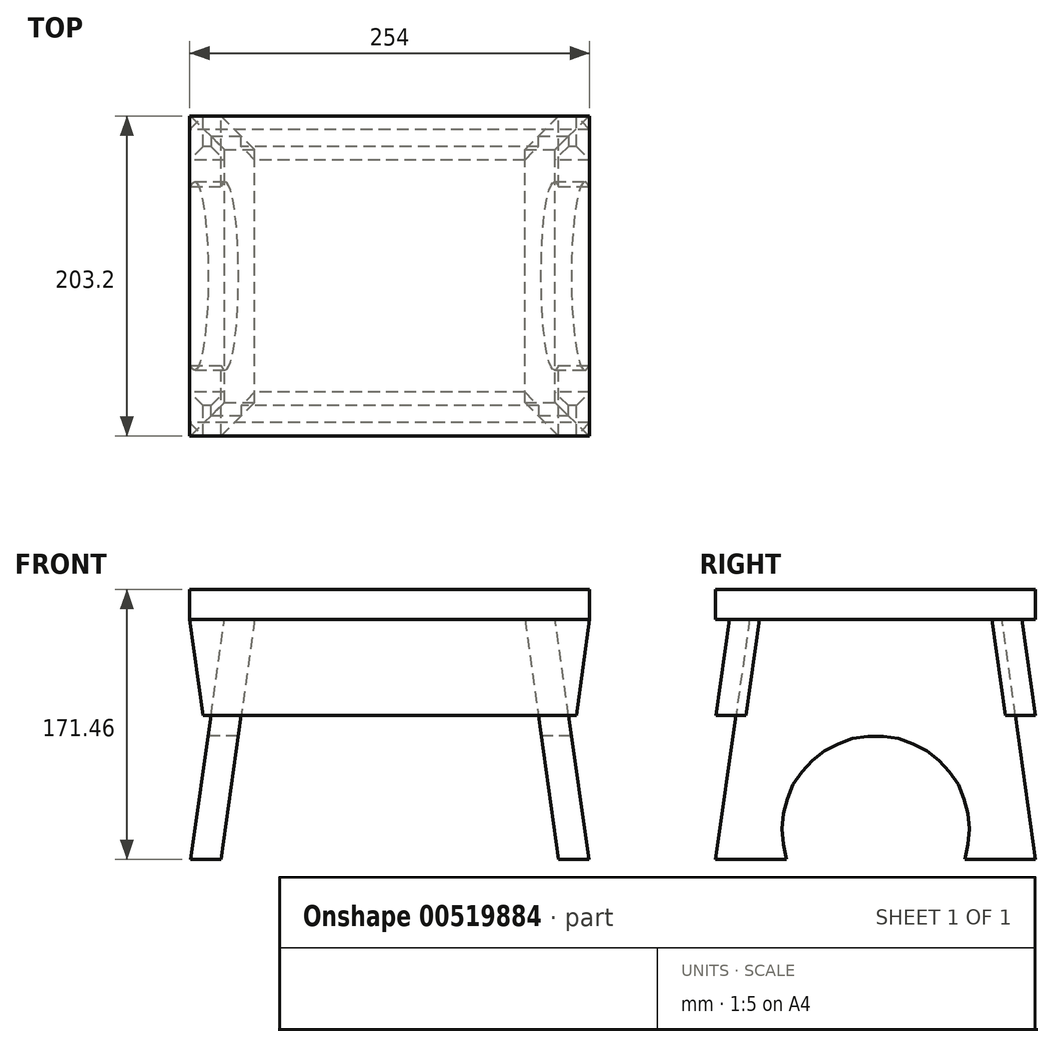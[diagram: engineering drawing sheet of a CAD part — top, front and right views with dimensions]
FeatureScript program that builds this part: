
annotation { "Feature Type Name" : "Feature", "Feature Type Description" : "" }
export const myFeature = defineFeature(function(context is Context, id is Id, definition is map)
    precondition{}
    {
        {
            var Q0;
            Q0=qCreatedBy(makeId("Front.planeOp"),FACE);
            var sketch = newSketch(context, id + "F0", { "sketchPlane" : qUnion([Q0])});
            skLineSegment(sketch, "E0.bottom", {"start": v(127, 9.53) * mm, "end": v(-127, 9.53) * mm});
            skLineSegment(sketch, "E0.top", {"start": v(127, -9.53) * mm, "end": v(-127, -9.53) * mm});
            skLineSegment(sketch, "E0.left", {"start": v(127, 9.53) * mm, "end": v(127, -9.52) * mm});
            skLineSegment(sketch, "E0.right", {"start": v(-127, 9.53) * mm, "end": v(-127, -9.52) * mm});
            skPoint(sketch, "E0.middle", {"position": v(0, 0) * mm});
            skLineSegment(sketch, "E1.bottom", {"start": v(-127, -9.53) * mm, "end": v(127, -9.53) * mm, "construction": true});
            skLineSegment(sketch, "E1.top", {"start": v(-127, -161.92) * mm, "end": v(127, -161.92) * mm, "construction": true});
            skLineSegment(sketch, "E1.left", {"start": v(-127, -9.52) * mm, "end": v(-127, -161.92) * mm, "construction": true});
            skLineSegment(sketch, "E1.right", {"start": v(127, -9.52) * mm, "end": v(127, -161.92) * mm, "construction": true});
            skLineSegment(sketch, "E2", {"start": v(105, -9.52) * mm, "end": v(126.42, -161.92) * mm});
            skLineSegment(sketch, "E3", {"start": v(126.42, -161.92) * mm, "end": v(107.18, -161.92) * mm});
            skLineSegment(sketch, "E4", {"start": v(107.18, -161.92) * mm, "end": v(85.76, -9.52) * mm});
            skLineSegment(sketch, "E5", {"start": v(0, -9.52) * mm, "end": v(0, -161.92) * mm});
            skLineSegment(sketch, "E6.MirrorCS", {"start": v(-107.18, -161.92) * mm, "end": v(-85.76, -9.52) * mm});
            skLineSegment(sketch, "E7.MirrorCS", {"start": v(-105, -9.52) * mm, "end": v(-126.42, -161.92) * mm});
            skLineSegment(sketch, "E8.MirrorCS", {"start": v(-126.42, -161.92) * mm, "end": v(-107.18, -161.92) * mm});
            skLineSegment(sketch, "E9.bottom", {"start": v(-127, -9.53) * mm, "end": v(127, -9.53) * mm});
            skLineSegment(sketch, "E9.top", {"start": v(-127, -70.48) * mm, "end": v(127, -70.48) * mm});
            skLineSegment(sketch, "E9.left", {"start": v(-127, -9.52) * mm, "end": v(-127, -70.48) * mm});
            skLineSegment(sketch, "E9.right", {"start": v(127, -9.52) * mm, "end": v(127, -70.48) * mm});
            skLineSegment(sketch, "E10", {"start": v(-127, -9.52) * mm, "end": v(-118.43, -70.48) * mm});
            skLineSegment(sketch, "E11.MirrorCS", {"start": v(127, -9.52) * mm, "end": v(118.43, -70.48) * mm});
            skSolve(sketch);
        }
        {
            var Q0;
            Q0=makeQuery(id+"F0.imprint","IMPRINT",FACE,{"disambiguationData":[TD([[makeQuery(id+"F0.imprint","IMPRINT",EDGE,{"derivedFrom":sQuery(id+"F0.wireOp",EDGE,"E0.bottom")}),1.0]])]});
            extrude(context, id + "F1", {"entities" : qUnion([Q0]), "endBound" : BoundingType.SYMMETRIC, "depth" : 203.2 * mm, "offsetDistance" : 25.4 * mm});
        }
        {
            var Q0;
            {var subQ0=sQuery(id+"F0.wireOp",EDGE,"E8.MirrorCS");Q0=makeQuery(id+"F0.imprint","IMPRINT",FACE,{"disambiguationData":[TD([[makeQuery(id+"F0.imprint","IMPRINT",EDGE,{"derivedFrom":subQ0}),1.0]])]});}
            var Q1;
            {var subQ0=sQuery(id+"F0.wireOp",EDGE,"E9.bottom");var subQ1=sQuery(id+"F0.wireOp",EDGE,"E6.MirrorCS");var subQ2=makeQuery(id+"F0.imprint","INTERSECT",VERTEX,{"derivedFrom":[subQ1,subQ0]});Q1=makeQuery(id+"F0.imprint","IMPRINT",FACE,{"disambiguationData":[TD([[makeQuery(id+"F0.imprint","IMPRINT",EDGE,{"disambiguationData":[TD([[subQ2,1.0]])],"derivedFrom":subQ1}),1.0]])]});}
            var Q2;
            {var subQ0=sQuery(id+"F0.wireOp",EDGE,"E9.bottom");var subQ1=sQuery(id+"F0.wireOp",EDGE,"E2");var subQ2=makeQuery(id+"F0.imprint","INTERSECT",VERTEX,{"derivedFrom":[subQ1,subQ0]});Q2=makeQuery(id+"F0.imprint","IMPRINT",FACE,{"disambiguationData":[TD([[makeQuery(id+"F0.imprint","IMPRINT",EDGE,{"disambiguationData":[TD([[subQ2,-1.0]])],"derivedFrom":subQ1}),-1.0]])]});}
            var Q3;
            {var subQ0=sQuery(id+"F0.wireOp",EDGE,"E3");Q3=makeQuery(id+"F0.imprint","IMPRINT",FACE,{"disambiguationData":[TD([[makeQuery(id+"F0.imprint","IMPRINT",EDGE,{"derivedFrom":subQ0}),-1.0]])]});}
            var Q4;
            Q4=makeQuery(id+"F1.opExtrude","CAP_VERTEX",VERTEX,{"disambiguationData":[OSD([sQuery(id+"F0.wireOp",EDGE,"E0.left"),sQuery(id+"F0.wireOp",EDGE,"E9.bottom"),sQuery(id+"F0.wireOp",EDGE,"E9.right"),sQuery(id+"F0.wireOp",EDGE,"E11.MirrorCS")])],"isStart":false});
            var Q5;
            Q5=makeQuery(id+"F1.opExtrude","CAP_VERTEX",VERTEX,{"disambiguationData":[OSD([sQuery(id+"F0.wireOp",EDGE,"E0.left"),sQuery(id+"F0.wireOp",EDGE,"E9.bottom"),sQuery(id+"F0.wireOp",EDGE,"E9.right"),sQuery(id+"F0.wireOp",EDGE,"E11.MirrorCS")])],"isStart":true});
            extrude(context, id + "F2", {"entities" : qUnion([Q0, Q1, Q2, Q3]), "endBound" : BoundingType.UP_TO_VERTEX, "depth" : 25.4 * mm, "endBoundEntityVertex" : qUnion([Q4]), "offsetDistance" : 25.4 * mm, "hasSecondDirection" : true, "secondDirectionBound" : SecondDirectionBoundingType.UP_TO_VERTEX, "secondDirectionOppositeDirection" : true, "secondDirectionDepth" : 101.35 * mm, "secondDirectionBoundEntityVertex" : qUnion([Q5])});
        }
        {
            var Q0;
            Q0=qCreatedBy(makeId("Right.planeOp"),FACE);
            var sketch = newSketch(context, id + "F3", { "sketchPlane" : qUnion([Q0])});
            skLineSegment(sketch, "E12.0.0", {"start": v(101.6, -9.53) * mm, "end": v(-101.6, -9.53) * mm});
            skLineSegment(sketch, "E12.0.1", {"start": v(-101.6, -9.53) * mm, "end": v(-101.6, -161.92) * mm});
            skLineSegment(sketch, "E12.0.2", {"start": v(-101.6, -161.92) * mm, "end": v(101.6, -161.92) * mm});
            skLineSegment(sketch, "E12.0.3", {"start": v(101.6, -161.92) * mm, "end": v(101.6, -9.53) * mm});
            skLineSegment(sketch, "E13", {"start": v(-101.6, -161.92) * mm, "end": v(-80.18, -9.53) * mm});
            skLineSegment(sketch, "E14.MirrorCS", {"start": v(101.6, -161.92) * mm, "end": v(80.18, -9.52) * mm});
            skArc(sketch, "E15", {"start": v(56.73, -161.92) * mm, "mid": v(0, -83.04) * mm, "end": v(-56.73, -161.92) * mm});
            skSolve(sketch);
        }
        {
            var Q0;
            {var subQ0=sQuery(id+"F3.wireOp",EDGE,"E12.0.1");Q0=makeQuery(id+"F3.imprint","IMPRINT",FACE,{"disambiguationData":[TD([[makeQuery(id+"F3.imprint","IMPRINT",EDGE,{"derivedFrom":subQ0}),1.0]])]});}
            var Q1;
            {var subQ0=sQuery(id+"F3.wireOp",EDGE,"RRh9Eklb-wDQN-sjUj-zd0E-6col0GpbWAWS");Q1=makeQuery(id+"F3.imprint","IMPRINT",FACE,{"disambiguationData":[TD([[makeQuery(id+"F3.imprint","IMPRINT",EDGE,{"derivedFrom":subQ0}),1.0]])]});}
            var Q2;
            {var subQ0=sQuery(id+"F3.wireOp",EDGE,"E12.0.3");Q2=makeQuery(id+"F3.imprint","IMPRINT",FACE,{"disambiguationData":[TD([[makeQuery(id+"F3.imprint","IMPRINT",EDGE,{"derivedFrom":subQ0}),1.0]])]});}
            extrude(context, id + "F4", {"entities" : qUnion([Q0, Q1, Q2]), "operationType" : NewBodyOperationType.REMOVE, "endBound" : BoundingType.THROUGH_ALL, "oppositeDirection" : true, "depth" : 283.46 * mm, "offsetDistance" : 25.4 * mm, "hasSecondDirection" : true, "secondDirectionBound" : SecondDirectionBoundingType.THROUGH_ALL, "secondDirectionOppositeDirection" : false, "secondDirectionDepth" : 25.4 * mm});
        }
        {
            var Q0;
            Q0=qCreatedBy(makeId("Right.planeOp"),FACE);
            var sketch = newSketch(context, id + "F5", { "sketchPlane" : qUnion([Q0])});
            skLineSegment(sketch, "E16", {"start": v(-82.34, -70.48) * mm, "end": v(-73.77, -9.52) * mm});
            skLineSegment(sketch, "E17", {"start": v(0, 0) * mm, "end": v(0, -70.48) * mm});
            skPoint(sketch, "E17.endSnap0", {"position": v(0, -9.52) * mm});
            skLineSegment(sketch, "E18", {"start": v(-82.34, -70.48) * mm, "end": v(0, -70.48) * mm, "construction": true});
            skLineSegment(sketch, "E19", {"start": v(-101.57, -70.48) * mm, "end": v(-82.34, -70.48) * mm});
            skLineSegment(sketch, "E20.MirrorCS", {"start": v(82.34, -70.48) * mm, "end": v(73.77, -9.52) * mm});
            skLineSegment(sketch, "E21.MirrorCS", {"start": v(101.57, -70.48) * mm, "end": v(82.34, -70.48) * mm});
            skLineSegment(sketch, "E22.MirrorCS", {"start": v(93, -9.52) * mm, "end": v(101.57, -70.48) * mm});
            skLineSegment(sketch, "E23.0", {"start": v(-80.18, -9.53) * mm, "end": v(80.18, -9.53) * mm});
            skLineSegment(sketch, "E24.MirrorCS", {"start": v(-93, -9.52) * mm, "end": v(-101.57, -70.48) * mm});
            skLineSegment(sketch, "E25", {"start": v(-93, -9.53) * mm, "end": v(-73.77, -9.52) * mm});
            skLineSegment(sketch, "E26", {"start": v(73.77, -9.52) * mm, "end": v(93, -9.52) * mm});
            skSolve(sketch);
        }
        {
            var Q0;
            {var subQ5=sQuery(id+"F5.wireOp",EDGE,"E22.MirrorCS");Q0=makeQuery(id+"F5.imprint","IMPRINT",FACE,{"disambiguationData":[TD([[makeQuery(id+"F5.imprint","IMPRINT",EDGE,{"derivedFrom":subQ5}),-1.0]])]});}
            var Q1;
            {var subQ2=sQuery(id+"F5.wireOp",EDGE,"E16");Q1=makeQuery(id+"F5.imprint","IMPRINT",FACE,{"disambiguationData":[TD([[makeQuery(id+"F5.imprint","IMPRINT",EDGE,{"derivedFrom":subQ2}),1.0]])]});}
            var Q2;
            {var subQ5=sQuery(id+"F5.wireOp",EDGE,"E20.MirrorCS");Q2=makeQuery(id+"F5.imprint","IMPRINT",FACE,{"disambiguationData":[TD([[makeQuery(id+"F5.imprint","IMPRINT",EDGE,{"derivedFrom":subQ5}),-1.0]])]});}
            extrude(context, id + "F6", {"entities" : qUnion([Q0, Q1, Q2]), "endBound" : BoundingType.SYMMETRIC, "depth" : 254 * mm, "offsetDistance" : 25.4 * mm, "hasSecondDirection" : true, "secondDirectionOppositeDirection" : true, "secondDirectionDepth" : 57.66 * mm});
        }
        {
            var Q0;
            Q0=makeQuery(id+"F2.opExtrude","SWEPT_BODY",BODY,{"disambiguationData":[OSD([sQuery(id+"F0.wireOp",EDGE,"E6.MirrorCS"),sQuery(id+"F0.wireOp",EDGE,"E7.MirrorCS"),sQuery(id+"F0.wireOp",EDGE,"E8.MirrorCS"),sQuery(id+"F0.wireOp",EDGE,"E9.bottom")])]});
            var Q1;
            Q1=makeQuery(id+"F6.opExtrude","SWEPT_BODY",BODY,{"disambiguationData":[OSD([sQuery(id+"F5.wireOp",EDGE,"18ab9ac2-430c-4776-9646-1a30380874a2.0"),sQuery(id+"F5.wireOp",EDGE,"E16"),sQuery(id+"F5.wireOp",EDGE,"69aQgQHQ-lhwv-fZtQ-g1e2-YuPWH7Kryl7J"),sQuery(id+"F5.wireOp",EDGE,"E19")])]});
            var Q2;
            Q2=makeQuery(id+"F6.opExtrude","SWEPT_BODY",BODY,{"disambiguationData":[OSD([sQuery(id+"F5.wireOp",EDGE,"00f90565-3496-451c-a71f-fb93ed5257f6.0"),sQuery(id+"F5.wireOp",EDGE,"18ab9ac2-430c-4776-9646-1a30380874a2.0"),sQuery(id+"F5.wireOp",EDGE,"E21.MirrorCS"),sQuery(id+"F5.wireOp",EDGE,"E22.MirrorCS")])]});
            booleanBodies(context, id + "F7", {"operationType" : BooleanOperationType.SUBTRACTION, "tools" : qUnion([Q0]), "targets" : qUnion([Q1, Q2]), "keepTools" : true});
        }
        {
            var Q0;
            Q0=makeQuery(id+"F2.opExtrude","SWEPT_BODY",BODY,{"disambiguationData":[OSD([sQuery(id+"F0.wireOp",EDGE,"E2"),sQuery(id+"F0.wireOp",EDGE,"E3"),sQuery(id+"F0.wireOp",EDGE,"E4"),sQuery(id+"F0.wireOp",EDGE,"E9.bottom")])]});
            var Q1;
            Q1=makeQuery(id+"F6.opExtrude","SWEPT_BODY",BODY,{"disambiguationData":[OSD([sQuery(id+"F5.wireOp",EDGE,"18ab9ac2-430c-4776-9646-1a30380874a2.0"),sQuery(id+"F5.wireOp",EDGE,"E16"),sQuery(id+"F5.wireOp",EDGE,"69aQgQHQ-lhwv-fZtQ-g1e2-YuPWH7Kryl7J"),sQuery(id+"F5.wireOp",EDGE,"E19")])]});
            var Q2;
            Q2=makeQuery(id+"F6.opExtrude","SWEPT_BODY",BODY,{"disambiguationData":[OSD([sQuery(id+"F5.wireOp",EDGE,"18ab9ac2-430c-4776-9646-1a30380874a2.0"),sQuery(id+"F5.wireOp",EDGE,"E20.MirrorCS"),sQuery(id+"F5.wireOp",EDGE,"E21.MirrorCS"),sQuery(id+"F5.wireOp",EDGE,"E22.MirrorCS")])]});
            booleanBodies(context, id + "F8", {"operationType" : BooleanOperationType.SUBTRACTION, "tools" : qUnion([Q0]), "targets" : qUnion([Q1, Q2]), "keepTools" : true});
        }
        {
            var Q0;
            {var subQ0=sQuery(id+"F3.wireOp",EDGE,"E15");Q0=makeQuery(id+"F3.imprint","IMPRINT",FACE,{"disambiguationData":[TD([[makeQuery(id+"F3.imprint","IMPRINT",EDGE,{"derivedFrom":subQ0}),1.0]])]});}
            extrude(context, id + "F9", {"entities" : qUnion([Q0]), "operationType" : NewBodyOperationType.REMOVE, "endBound" : BoundingType.THROUGH_ALL, "oppositeDirection" : true, "depth" : 25.4 * mm, "offsetDistance" : 25.4 * mm, "hasSecondDirection" : true, "secondDirectionBound" : SecondDirectionBoundingType.THROUGH_ALL, "secondDirectionOppositeDirection" : false, "secondDirectionDepth" : 25.4 * mm});
        }
        {
            var Q0;
            {var subQ0=sQuery(id+"F0.wireOp",EDGE,"E9.right");Q0=makeQuery(id+"F0.imprint","IMPRINT",FACE,{"disambiguationData":[TD([[makeQuery(id+"F0.imprint","IMPRINT",EDGE,{"derivedFrom":subQ0}),-1.0]])]});}
            var Q1;
            {var subQ0=sQuery(id+"F0.wireOp",EDGE,"E9.left");Q1=makeQuery(id+"F0.imprint","IMPRINT",FACE,{"disambiguationData":[TD([[makeQuery(id+"F0.imprint","IMPRINT",EDGE,{"derivedFrom":subQ0}),1.0]])]});}
            extrude(context, id + "F10", {"entities" : qUnion([Q0, Q1]), "operationType" : NewBodyOperationType.REMOVE, "endBound" : BoundingType.THROUGH_ALL, "depth" : 25.4 * mm, "offsetDistance" : 25.4 * mm, "hasSecondDirection" : true, "secondDirectionBound" : SecondDirectionBoundingType.THROUGH_ALL, "secondDirectionOppositeDirection" : true, "secondDirectionDepth" : 25.4 * mm});
        }
    });
